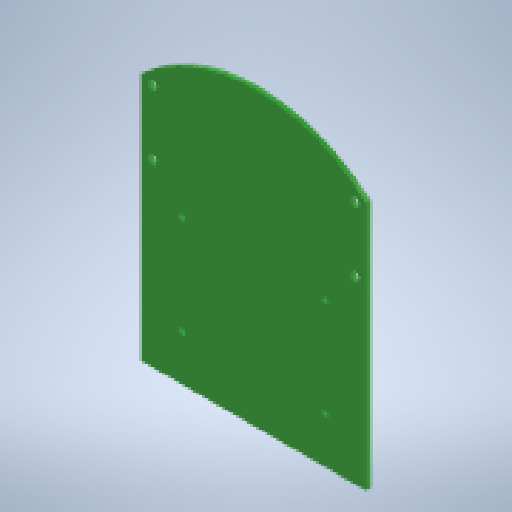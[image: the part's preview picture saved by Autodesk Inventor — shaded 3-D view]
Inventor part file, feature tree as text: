
AUTODESK INVENTOR PART (.ipt)
format: ipt  version: 2025.3 (Build 293356000, 356)  size: 145,408 bytes
history: native  units: mm
features: sketch x3, hole x2, other x1, extrude x1
ambient origin geometry x8: Origin, YZ Plane, XZ Plane, XY Plane, X Axis, Y Axis, Z Axis, Center Point
bodies: Body1 (feature_tree)
feature tree (7):
  other  "ソリッド1"
  extrude  "基板"  Depth=120.0mm
  hole  "モータ取付穴"  [1 undecoded]
  hole  "連結穴"  [1 undecoded]
  sketch  "スケッチ1"
  sketch  "スケッチ2"
  sketch  "スケッチ6"
note: 2 required parameter values undecoded (feature->parameter linkage not recoverable at this tier; creation-order binding heuristic only, values carry confidence <= 0.55)
